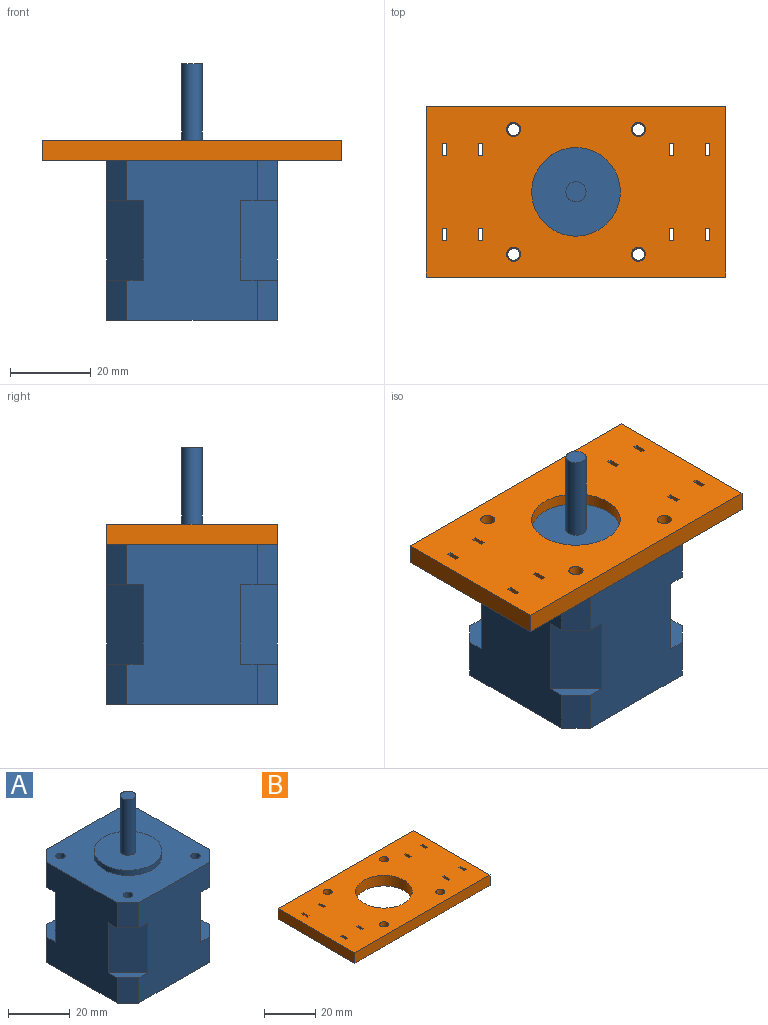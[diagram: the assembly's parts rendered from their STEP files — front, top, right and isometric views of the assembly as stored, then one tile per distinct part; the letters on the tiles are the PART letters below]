
ASSEMBLY  parts=2 mates=1
PART A: 38 faces, bbox 42.3x42.3x63.8 mm
  f0: plane 9x9mm, normal (0,0,1), area 28mm2, adj f6,f7,f10,f33
  f1: plane 9x9mm, normal (0,0,1), area 28mm2, adj f5,f6,f9,f30
  f2: plane 9x9mm, normal (0,0,1), area 28mm2, adj f4,f5,f12,f31
  f3: plane 9x9mm, normal (0,0,1), area 28mm2, adj f4,f7,f11,f32
  f4: plane 39.8x32.3mm, normal (1,0,0), area 1127.1mm2, adj f2,f3,f8,f11,f12,f18,f19,f21
  f5: plane 39.8x32.3mm, normal (0,1,0), area 1127.1mm2, adj f1,f2,f8,f9,f12,f19,f20,f21
  f6: plane 39.8x32.3mm, normal (-1,0,0), area 1127.1mm2, adj f0,f1,f8,f9,f10,f17,f20,f21
  f7: plane 39.8x32.3mm, normal (0,-1,0), area 1127.1mm2, adj f0,f3,f8,f10,f11,f17,f18,f21
  f8: plane 42.3x42.3mm, normal (0,0,-1), area 1711mm2, adj f4,f5,f6,f7,f9,f10,f11,f12
  f9: plane 10x5mm, normal (-0.71,0.71,0), area 70.7mm2, adj f1,f5,f6,f8
  f10: plane 10x5mm, normal (-0.71,-0.71,0), area 70.7mm2, adj f0,f6,f7,f8
  f11: plane 10x5mm, normal (0.71,-0.71,0), area 70.7mm2, adj f3,f4,f7,f8
  f12: plane 10x5mm, normal (0.71,0.71,0), area 70.7mm2, adj f2,f4,f5,f8
  f13: cylinder r=1.5mm len=39.8mm, axis (0,0,1), area 375.1mm2, adj f8,f21
  f14: cylinder r=1.5mm len=39.8mm, axis (0,0,1), area 375.1mm2, adj f8,f21
  f15: cylinder r=1.5mm len=39.8mm, axis (0,0,1), area 375.1mm2, adj f8,f21
  f16: cylinder r=1.5mm len=39.8mm, axis (0,0,1), area 375.1mm2, adj f8,f21
  f17: plane 9x9mm, normal (0,0,-1), area 28mm2, adj f6,f7,f23,f33
  f18: plane 9x9mm, normal (0,0,-1), area 28mm2, adj f4,f7,f22,f32
  f19: plane 9x9mm, normal (0,0,-1), area 28mm2, adj f4,f5,f25,f31
  f20: plane 9x9mm, normal (0,0,-1), area 28mm2, adj f5,f6,f24,f30
  f21: plane 42.3x42.3mm, normal (0,0,1), area 1330.9mm2, adj f4,f5,f6,f7,f13,f14,f15,f16
  f22: plane 10x5mm, normal (0.71,-0.71,0), area 70.7mm2, adj f4,f7,f18,f21
  f23: plane 10x5mm, normal (-0.71,-0.71,0), area 70.7mm2, adj f6,f7,f17,f21
  f24: plane 10x5mm, normal (-0.71,0.71,0), area 70.7mm2, adj f5,f6,f20,f21
  f25: plane 10x5mm, normal (0.71,0.71,0), area 70.7mm2, adj f4,f5,f19,f21
  f26: cylinder r=11mm len=22mm, axis (0,0,-1), area 138.2mm2, adj f21,f27
  f27: plane 22x22mm, normal (0,0,1), area 360.5mm2, adj f26,f28
  f28: cylinder r=2.5mm len=22mm, axis (0,0,-1), area 345.6mm2, adj f27,f29
  f29: plane 5x5mm, normal (0,0,1), area 19.6mm2, adj f28
  f30: plane 19.8x9mm, normal (-0.71,0.71,0), area 252mm2, adj f1,f5,f6,f20
  f31: plane 19.8x9mm, normal (0.71,0.71,0), area 252mm2, adj f2,f4,f5,f19
  f32: plane 19.8x9mm, normal (0.71,-0.71,0), area 252mm2, adj f3,f4,f7,f18
  f33: plane 19.8x9mm, normal (-0.71,-0.71,0), area 252mm2, adj f0,f6,f7,f17
  f34: plane 25x3mm, normal (0,1,0), area 75mm2, adj f35,f36,f37
  f35: cylinder r=2.5mm len=25mm, axis (0,0,1), area 80.4mm2, adj f34,f36,f37
  f36: plane 3x0.5mm, normal (0,0,1), area 1mm2, adj f34,f35
  f37: plane 3x0.5mm, normal (0,0,-1), area 1mm2, adj f34,f35
PART B: 43 faces, bbox 74.3x42.3x5 mm
  f0: plane 74.3x5mm, normal (0,1,0), area 371.5mm2, adj f1,f40,f41,f42
  f1: plane 42.3x5mm, normal (-1,0,0), area 211.5mm2, adj f0,f2,f41,f42
  f2: plane 74.3x5mm, normal (0,-1,0), area 371.5mm2, adj f1,f40,f41,f42
  f3: plane 5x3mm, normal (1,0,0), area 15mm2, adj f4,f27,f41,f42
  f4: plane 5x1mm, normal (0,-1,0), area 5mm2, adj f3,f5,f41,f42
  f5: plane 5x3mm, normal (-1,0,0), area 15mm2, adj f4,f27,f41,f42
  f6: plane 5x3mm, normal (1,0,0), area 15mm2, adj f7,f28,f41,f42
  f7: plane 5x1mm, normal (0,-1,0), area 5mm2, adj f6,f8,f41,f42
  f8: plane 5x3mm, normal (-1,0,0), area 15mm2, adj f7,f28,f41,f42
  f9: plane 5x3mm, normal (1,0,0), area 15mm2, adj f10,f29,f41,f42
  f10: plane 5x1mm, normal (0,-1,0), area 5mm2, adj f9,f11,f41,f42
  f11: plane 5x3mm, normal (-1,0,0), area 15mm2, adj f10,f29,f41,f42
  f12: plane 5x1mm, normal (0,1,0), area 5mm2, adj f13,f35,f41,f42
  f13: plane 5x3mm, normal (1,0,0), area 15mm2, adj f12,f14,f41,f42
  f14: plane 5x1mm, normal (0,-1,0), area 5mm2, adj f13,f35,f41,f42
  f15: plane 5x3mm, normal (-1,0,0), area 15mm2, adj f16,f36,f41,f42
  f16: plane 5x1mm, normal (0,1,0), area 5mm2, adj f15,f17,f41,f42
  f17: plane 5x3mm, normal (1,0,0), area 15mm2, adj f16,f36,f41,f42
  f18: plane 5x1mm, normal (0,1,0), area 5mm2, adj f19,f37,f41,f42
  f19: plane 5x3mm, normal (1,0,0), area 15mm2, adj f18,f20,f41,f42
  f20: plane 5x1mm, normal (0,-1,0), area 5mm2, adj f19,f37,f41,f42
  f21: plane 5x3mm, normal (1,0,0), area 15mm2, adj f22,f38,f41,f42
  f22: plane 5x1mm, normal (0,-1,0), area 5mm2, adj f21,f23,f41,f42
  f23: plane 5x3mm, normal (-1,0,0), area 15mm2, adj f22,f38,f41,f42
  f24: plane 5x1mm, normal (0,-1,0), area 5mm2, adj f25,f39,f41,f42
  f25: plane 5x3mm, normal (-1,0,0), area 15mm2, adj f24,f26,f41,f42
  f26: plane 5x1mm, normal (0,1,0), area 5mm2, adj f25,f39,f41,f42
  f27: plane 5x1mm, normal (0,1,0), area 5mm2, adj f3,f5,f41,f42
  f28: plane 5x1mm, normal (0,1,0), area 5mm2, adj f6,f8,f41,f42
  f29: plane 5x1mm, normal (0,1,0), area 5mm2, adj f9,f11,f41,f42
  f30: cylinder r=11mm len=22mm, axis (0,0,-1), area 345.6mm2, adj f41,f42
  f31: cylinder r=1.75mm len=5mm, axis (0,0,-1), area 55mm2, adj f41,f42
  f32: cylinder r=1.75mm len=5mm, axis (0,0,-1), area 55mm2, adj f41,f42
  f33: cylinder r=1.75mm len=5mm, axis (0,0,-1), area 55mm2, adj f41,f42
  f34: cylinder r=1.75mm len=5mm, axis (0,0,-1), area 55mm2, adj f41,f42
  f35: plane 5x3mm, normal (-1,0,0), area 15mm2, adj f12,f14,f41,f42
  f36: plane 5x1mm, normal (0,-1,0), area 5mm2, adj f15,f17,f41,f42
  f37: plane 5x3mm, normal (-1,0,0), area 15mm2, adj f18,f20,f41,f42
  f38: plane 5x1mm, normal (0,1,0), area 5mm2, adj f21,f23,f41,f42
  f39: plane 5x3mm, normal (1,0,0), area 15mm2, adj f24,f26,f41,f42
  f40: plane 42.3x5mm, normal (1,0,0), area 211.5mm2, adj f0,f2,f41,f42
  f41: plane 74.3x42.3mm, normal (0,0,1), area 2700.3mm2, adj f0,f1,f2,f3,f4,f5,f6,f7
  f42: plane 74.3x42.3mm, normal (0,0,-1), area 2700.3mm2, adj f0,f1,f2,f3,f4,f5,f6,f7
PLACE A t=(-2.95,31.11,6.93)mm
PLACE B t=(-2.95,31.11,46.73)mm
MATE fastened A.f15 <-> B.f33  axis (0,0,1) through (12.55,15.61,46.73)mm
